# Revit family: LCOMN Square Intellect
name_source: partatom
category: Lighting Fixtures
units: mm (PartAtom-declared; Revit-internal decimal feet)

## family parameters
Always vertical = Yes
Cut with Voids When Loaded = No
Host = Ceiling
Light Source = Yes
OmniClass Number = 23.80.70.11.14.11
OmniClass Title = Downlights
Part Type = Normal
Room Calculation Point = No
Round Connector Dimension = Use Diameter
Shared = No

## types (5) — shared parameters
Assembly Code = D5020200
Color Filter = 16777215
Description = Intellect Enabled LED Commercial Type N Square
Dimming Lamp Color Temperature Shift = <None>
Housing Finish = Metal - Viscor - White
Lamp = LED
Lens Finsih = Polycarbonate - Viscor - Frosted Square
Manufacturer = VISIONEERING by VISCOR
Model = LCOMN SQ Intellect
Tilt Angle = 90.00°
URL = https://www.viscor.com
Voltage = 120 V
Width = 0' - 2 1/16"

## per-type parameters (varying)
| type | Apparent Load | Emit from Line Length | Lamp Wattage | Length | Photometric Web File |
| LCOMN24-LED840K020LUNV-P95V99(LV01) | 17 VA | 1' - 10 7/8" | 17 VA | 1' - 10 7/8" | LCOMN24-LED840K020LUNV-P95V99(LV01).IES |
| LCOMN48-LED840K020LUNV-P95V99(LV01) | 18 VA | 3' - 8 7/8" | 18 VA | 3' - 8 7/8" | LCOMN48-LED840K020LUNV-P95V99(LV01).ies |
| LCOMN48-LED840K040LUNV-P95V99(LV01) | 33 VA | 3' - 8 7/8" | 33 VA | 3' - 8 7/8" | LCOMN48-LED840K040LUNV-P95V99(LV01).ies |
| LCOMN96-LED840K040LUNV-P95V99(LV01) | 32 VA | 7' - 5 1/4" | 32 VA | 7' - 5 1/4" | LCOMN96-LED840K040LUNV-P95V99(LV01).ies |
| LCOMN96-LED840K080LUNV-P95V99(LV01) | 65 VA | 7' - 5 1/4" | 65 VA | 7' - 5 1/4" | LCOMN96-LED840K080LUNV-P95V99(LV01).ies |

## geometry (parser evidence)
native form markers: Sweep x2
no freeform markers — native parametric forms only
